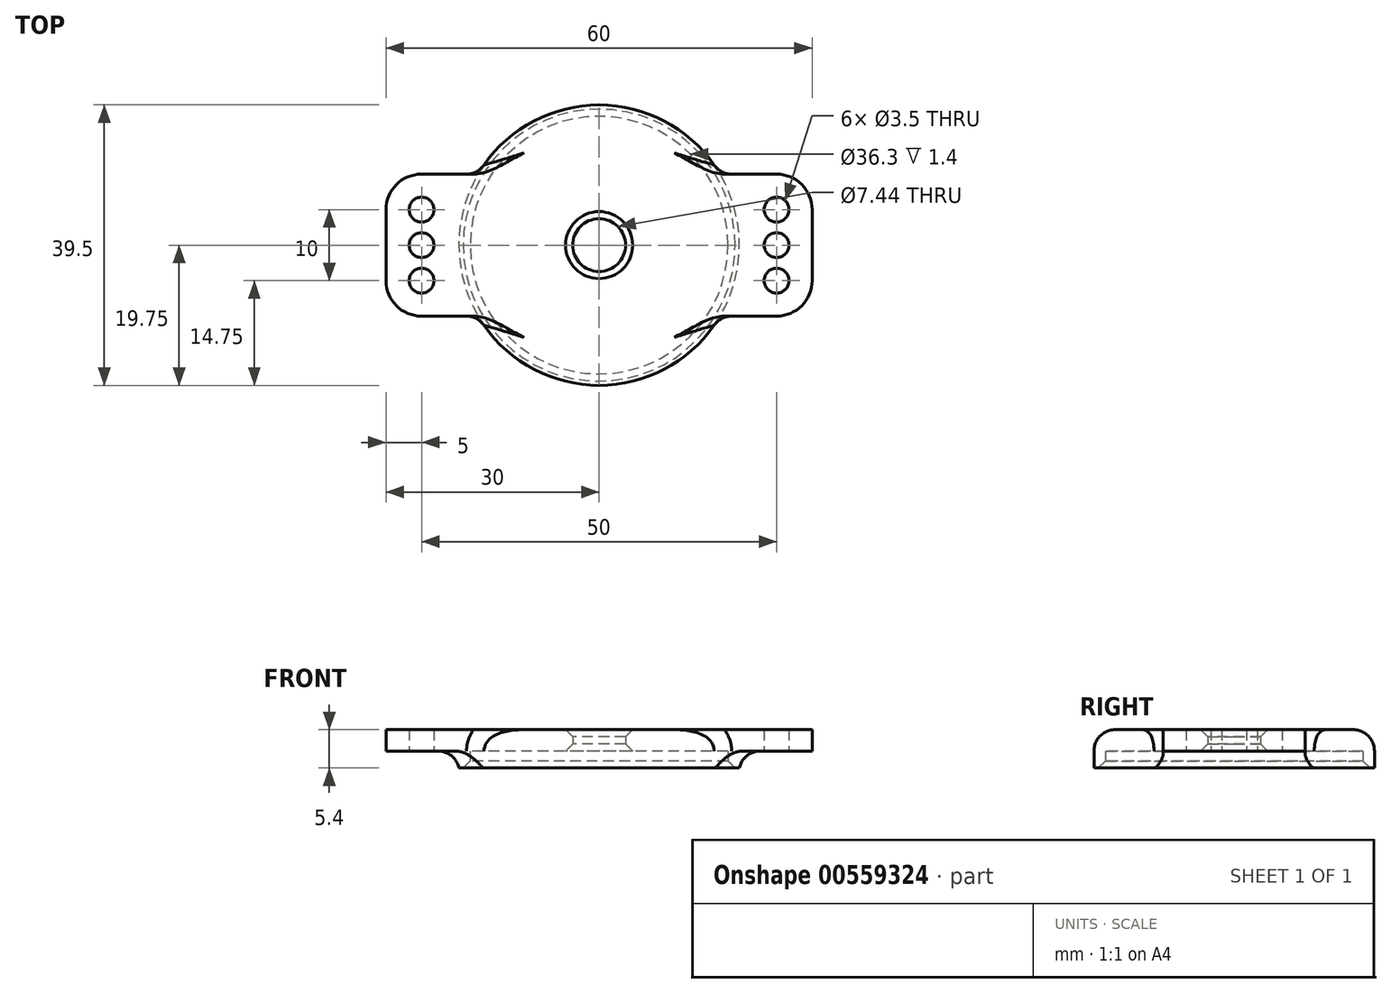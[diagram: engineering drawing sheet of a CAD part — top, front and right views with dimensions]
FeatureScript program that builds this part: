
annotation { "Feature Type Name" : "Feature", "Feature Type Description" : "" }
export const myFeature = defineFeature(function(context is Context, id is Id, definition is map)
    precondition{}
    {
        {
            var Q0;
            Q0=qCreatedBy(makeId("Top.planeOp"),FACE);
            var sketch = newSketch(context, id + "F0", { "sketchPlane" : qUnion([Q0])});
            skCircle(sketch, "E0", {"center": v(0, 0) * mm, "radius": 18.15 * mm});
            skCircle(sketch, "E1", {"center": v(0, 0) * mm, "radius": 19.75 * mm});
            skSolve(sketch);
        }
        {
            var Q0;
            Q0 = qSketchRegion(id + "F0", true);
            extrude(context, id + "F1", {"entities" : qUnion([Q0]), "depth" : 2.4 * mm, "offsetDistance" : 25 * mm});
        }
        {
            var Q0;
            Q0=makeQuery(id+"F1.opExtrude","CAP_FACE",FACE,{"disambiguationData":[OSD([sQuery(id+"F0.wireOp",EDGE,"E0"),sQuery(id+"F0.wireOp",EDGE,"E1")])],"isStart":false});
            var sketch = newSketch(context, id + "F2", { "sketchPlane" : qUnion([Q0])});
            skCircle(sketch, "E2", {"center": v(0, 0) * mm, "radius": 3.72 * mm});
            skLineSegment(sketch, "E3", {"start": v(0, 0) * mm, "end": v(25, 0) * mm, "construction": true});
            skLineSegment(sketch, "E4", {"start": v(0, 0) * mm, "end": v(-25, 0) * mm, "construction": true});
            skLineSegment(sketch, "E5", {"start": v(-25, 0) * mm, "end": v(-25, -5) * mm, "construction": true});
            skLineSegment(sketch, "E6", {"start": v(-25, 0) * mm, "end": v(-25, 5) * mm, "construction": true});
            skCircle(sketch, "E7", {"center": v(-25, 0) * mm, "radius": 1.75 * mm});
            skCircle(sketch, "E8", {"center": v(-25, 5) * mm, "radius": 1.75 * mm});
            skCircle(sketch, "E9", {"center": v(-25, -5) * mm, "radius": 1.75 * mm});
            skLineSegment(sketch, "E10", {"start": v(-25, 5) * mm, "end": v(-25, 10) * mm, "construction": true});
            skLineSegment(sketch, "E11", {"start": v(-25, -5) * mm, "end": v(-25, -10) * mm, "construction": true});
            skLineSegment(sketch, "E12", {"start": v(-17.03, 10) * mm, "end": v(-17.03, 10) * mm});
            skArc(sketch, "E13", {"start": v(-17.03, -10) * mm, "mid": v(19.75, 0) * mm, "end": v(-17.03, 10) * mm});
            skLineSegment(sketch, "E14", {"start": v(-25, 0) * mm, "end": v(-30, 0) * mm, "construction": true});
            skLineSegment(sketch, "E15", {"start": v(-30, 10) * mm, "end": v(-17.03, 10) * mm});
            skLineSegment(sketch, "E16", {"start": v(-17.03, -10) * mm, "end": v(-30, -10) * mm});
            skLineSegment(sketch, "E17", {"start": v(-30, -10) * mm, "end": v(-30, 10) * mm});
            skCircle(sketch, "E18.MirrorC", {"center": v(25, 0) * mm, "radius": 1.75 * mm});
            skCircle(sketch, "E19.MirrorC", {"center": v(25, -5) * mm, "radius": 1.75 * mm});
            skCircle(sketch, "E20.MirrorC", {"center": v(25, 5) * mm, "radius": 1.75 * mm});
            skLineSegment(sketch, "E21.MirrorCS", {"start": v(30, -10) * mm, "end": v(30, 10) * mm});
            skLineSegment(sketch, "E22.MirrorCS", {"start": v(30, 10) * mm, "end": v(17.03, 10) * mm});
            skLineSegment(sketch, "E23.MirrorCS", {"start": v(17.03, -10) * mm, "end": v(30, -10) * mm});
            skSolve(sketch);
        }
        {
            var Q0;
            Q0 = qSketchRegion(id + "F2", true);
            extrude(context, id + "F3", {"entities" : qUnion([Q0]), "operationType" : NewBodyOperationType.ADD, "depth" : 3 * mm, "offsetDistance" : 25 * mm});
        }
        {
            var Q0;
            Q0=makeQuery(id+"F3.opExtrude","CAP_EDGE",EDGE,{"disambiguationData":[OSD([sQuery(id+"F2.wireOp",EDGE,"E2")])],"isStart":true});
            var Q1;
            Q1=makeQuery(id+"F3.opExtrude","CAP_EDGE",EDGE,{"disambiguationData":[OSD([sQuery(id+"F2.wireOp",EDGE,"E2")])],"isStart":false});
            var Q2;
            Q2=makeQuery(id+"F1.opExtrude","CAP_EDGE",EDGE,{"disambiguationData":[OSD([sQuery(id+"F0.wireOp",EDGE,"E0")])],"isStart":true});
            chamfer(context, id + "F4", {"entities" : qUnion([Q0, Q1, Q2]), "width" : 1 * mm, "tangentPropagation" : true});
        }
        {
            var Q0;
            {var subQ2=sQuery(id+"F0.wireOp",EDGE,"E1");var subQ3=makeQuery(id+"F1.opExtrude","CAP_EDGE",EDGE,{"disambiguationData":[OSD([subQ2])],"isStart":false});var subQ5=sQuery(id+"F2.wireOp",EDGE,"E22.MirrorCS");Q0=makeQuery(id+"F3.boolean.opBoolean","SPLIT",EDGE,{"disambiguationData":[TD([makeQuery(id+"F3.opExtrude","SWEPT_FACE",FACE,{"disambiguationData":[OSD([subQ5])]})])],"derivedFrom":subQ3});}
            var Q1;
            {var subQ2=sQuery(id+"F0.wireOp",EDGE,"E1");var subQ3=makeQuery(id+"F1.opExtrude","CAP_EDGE",EDGE,{"disambiguationData":[OSD([subQ2])],"isStart":false});var subQ6=sQuery(id+"F2.wireOp",EDGE,"E15");Q1=makeQuery(id+"F3.boolean.opBoolean","SPLIT",EDGE,{"disambiguationData":[TD([makeQuery(id+"F3.opExtrude","SWEPT_FACE",FACE,{"disambiguationData":[OSD([subQ6])]})])],"derivedFrom":subQ3});}
            var Q2;
            {var subQ0=sQuery(id+"F2.wireOp",EDGE,"E13");Q2=makeQuery(id+"F3.opExtrude","CAP_EDGE",EDGE,{"disambiguationData":[OSD([subQ0]),TDD([makeQuery(id+"F2.imprint","IMPRINT",EDGE,{"disambiguationData":[TD([[makeQuery(id+"F2.imprint","INTERSECT",VERTEX,{"derivedFrom":[subQ0,sQuery(id+"F2.wireOp",EDGE,"E23.MirrorCS")]}),1.0]])],"derivedFrom":subQ0})])],"isStart":false});}
            var Q3;
            {var subQ0=sQuery(id+"F2.wireOp",EDGE,"E13");Q3=makeQuery(id+"F3.opExtrude","CAP_EDGE",EDGE,{"disambiguationData":[OSD([subQ0]),TDD([makeQuery(id+"F2.imprint","IMPRINT",EDGE,{"disambiguationData":[TD([[makeQuery(id+"F2.imprint","INTERSECT",VERTEX,{"derivedFrom":[subQ0,sQuery(id+"F2.wireOp",EDGE,"E22.MirrorCS")]}),-1.0]])],"derivedFrom":subQ0})])],"isStart":false});}
            fillet(context, id + "F5", {"entities" : qUnion([Q0, Q1, Q2, Q3]), "radius" : 3 * mm, "tangentPropagation" : true, "allowEdgeOverflow" : false});
        }
        {
            var Q0;
            Q0=makeQuery(id+"F5.opFillet","TWEAK_EDGE",EDGE,{"derivedFrom":[makeQuery(id+"F3.opExtrude","CAP_VERTEX",VERTEX,{"disambiguationData":[OSD([sQuery(id+"F2.wireOp",EDGE,"E13"),sQuery(id+"F2.wireOp",EDGE,"E23.MirrorCS")])],"isStart":true})]});
            var Q1;
            {var subQ0=sQuery(id+"F2.wireOp",EDGE,"E23.MirrorCS");var subQ1=sQuery(id+"F2.wireOp",EDGE,"E13");Q1=makeQuery(id+"F5.opFillet","BLEND_EDGE",EDGE,{"blendedFrom":[makeQuery(id+"F3.opExtrude","CAP_EDGE",EDGE,{"disambiguationData":[OSD([subQ1]),TDD([makeQuery(id+"F2.imprint","IMPRINT",EDGE,{"disambiguationData":[TD([[makeQuery(id+"F2.imprint","INTERSECT",VERTEX,{"derivedFrom":[subQ1,subQ0]}),1.0]])],"derivedFrom":subQ1})])],"isStart":false}),makeQuery(id+"F3.opExtrude","SWEPT_FACE",FACE,{"disambiguationData":[OSD([subQ0])]})],"blendedInto":[makeQuery(id+"F3.opExtrude","SWEPT_FACE",FACE,{"disambiguationData":[OSD([subQ0])]})]});}
            var Q2;
            {var subQ0=sQuery(id+"F2.wireOp",EDGE,"E16");var subQ1=sQuery(id+"F2.wireOp",EDGE,"E13");Q2=makeQuery(id+"F5.opFillet","BLEND_EDGE",EDGE,{"blendedFrom":[makeQuery(id+"F3.opExtrude","CAP_EDGE",EDGE,{"disambiguationData":[OSD([subQ1]),TDD([makeQuery(id+"F2.imprint","IMPRINT",EDGE,{"disambiguationData":[TD([[makeQuery(id+"F2.imprint","INTERSECT",VERTEX,{"derivedFrom":[subQ1,sQuery(id+"F2.wireOp",EDGE,"E23.MirrorCS")]}),1.0]])],"derivedFrom":subQ1})])],"isStart":false}),makeQuery(id+"F3.opExtrude","SWEPT_FACE",FACE,{"disambiguationData":[OSD([subQ0])]})],"blendedInto":[makeQuery(id+"F3.opExtrude","SWEPT_FACE",FACE,{"disambiguationData":[OSD([subQ0])]})]});}
            var Q3;
            Q3=makeQuery(id+"F5.opFillet","TWEAK_EDGE",EDGE,{"derivedFrom":[makeQuery(id+"F3.opExtrude","CAP_VERTEX",VERTEX,{"disambiguationData":[OSD([sQuery(id+"F0.wireOp",EDGE,"E1"),sQuery(id+"F2.wireOp",EDGE,"E13"),sQuery(id+"F2.wireOp",EDGE,"E16")])],"isStart":true})]});
            var Q4;
            Q4=makeQuery(id+"F5.opFillet","TWEAK_EDGE",EDGE,{"derivedFrom":[makeQuery(id+"F3.opExtrude","CAP_VERTEX",VERTEX,{"disambiguationData":[OSD([sQuery(id+"F0.wireOp",EDGE,"E1"),sQuery(id+"F2.wireOp",EDGE,"E13"),sQuery(id+"F2.wireOp",EDGE,"E15")])],"isStart":true})]});
            var Q5;
            {var subQ0=sQuery(id+"F2.wireOp",EDGE,"E15");var subQ1=sQuery(id+"F2.wireOp",EDGE,"E13");Q5=makeQuery(id+"F5.opFillet","BLEND_EDGE",EDGE,{"blendedFrom":[makeQuery(id+"F3.opExtrude","CAP_EDGE",EDGE,{"disambiguationData":[OSD([subQ1]),TDD([makeQuery(id+"F2.imprint","IMPRINT",EDGE,{"disambiguationData":[TD([[makeQuery(id+"F2.imprint","INTERSECT",VERTEX,{"derivedFrom":[subQ1,sQuery(id+"F2.wireOp",EDGE,"E22.MirrorCS")]}),-1.0]])],"derivedFrom":subQ1})])],"isStart":false}),makeQuery(id+"F3.opExtrude","SWEPT_FACE",FACE,{"disambiguationData":[OSD([subQ0])]})],"blendedInto":[makeQuery(id+"F3.opExtrude","SWEPT_FACE",FACE,{"disambiguationData":[OSD([subQ0])]})]});}
            var Q6;
            Q6=makeQuery(id+"F5.opFillet","TWEAK_EDGE",EDGE,{"derivedFrom":[makeQuery(id+"F3.opExtrude","CAP_VERTEX",VERTEX,{"disambiguationData":[OSD([sQuery(id+"F2.wireOp",EDGE,"E13"),sQuery(id+"F2.wireOp",EDGE,"E22.MirrorCS")])],"isStart":true})]});
            var Q7;
            {var subQ0=sQuery(id+"F2.wireOp",EDGE,"E22.MirrorCS");var subQ1=sQuery(id+"F2.wireOp",EDGE,"E13");Q7=makeQuery(id+"F5.opFillet","BLEND_EDGE",EDGE,{"blendedFrom":[makeQuery(id+"F3.opExtrude","CAP_EDGE",EDGE,{"disambiguationData":[OSD([subQ1]),TDD([makeQuery(id+"F2.imprint","IMPRINT",EDGE,{"disambiguationData":[TD([[makeQuery(id+"F2.imprint","INTERSECT",VERTEX,{"derivedFrom":[subQ1,subQ0]}),-1.0]])],"derivedFrom":subQ1})])],"isStart":false}),makeQuery(id+"F3.opExtrude","SWEPT_FACE",FACE,{"disambiguationData":[OSD([subQ0])]})],"blendedInto":[makeQuery(id+"F3.opExtrude","SWEPT_FACE",FACE,{"disambiguationData":[OSD([subQ0])]})]});}
            fillet(context, id + "F6", {"entities" : qUnion([Q0, Q1, Q2, Q3, Q4, Q5, Q6, Q7]), "radius" : 3 * mm, "tangentPropagation" : true, "allowEdgeOverflow" : false});
        }
        {
            var Q0;
            Q0=makeQuery(id+"F3.opExtrude","SWEPT_EDGE",EDGE,{"disambiguationData":[OSD([sQuery(id+"F2.wireOp",EDGE,"E15"),sQuery(id+"F2.wireOp",EDGE,"E17")])]});
            var Q1;
            Q1=makeQuery(id+"F3.opExtrude","SWEPT_EDGE",EDGE,{"disambiguationData":[OSD([sQuery(id+"F2.wireOp",EDGE,"E16"),sQuery(id+"F2.wireOp",EDGE,"E17")])]});
            var Q2;
            Q2=makeQuery(id+"F3.opExtrude","SWEPT_EDGE",EDGE,{"disambiguationData":[OSD([sQuery(id+"F2.wireOp",EDGE,"E21.MirrorCS"),sQuery(id+"F2.wireOp",EDGE,"E22.MirrorCS")])]});
            var Q3;
            Q3=makeQuery(id+"F3.opExtrude","SWEPT_EDGE",EDGE,{"disambiguationData":[OSD([sQuery(id+"F2.wireOp",EDGE,"E21.MirrorCS"),sQuery(id+"F2.wireOp",EDGE,"E23.MirrorCS")])]});
            fillet(context, id + "F7", {"entities" : qUnion([Q0, Q1, Q2, Q3]), "radius" : 5 * mm, "tangentPropagation" : true, "allowEdgeOverflow" : false});
        }
    });
